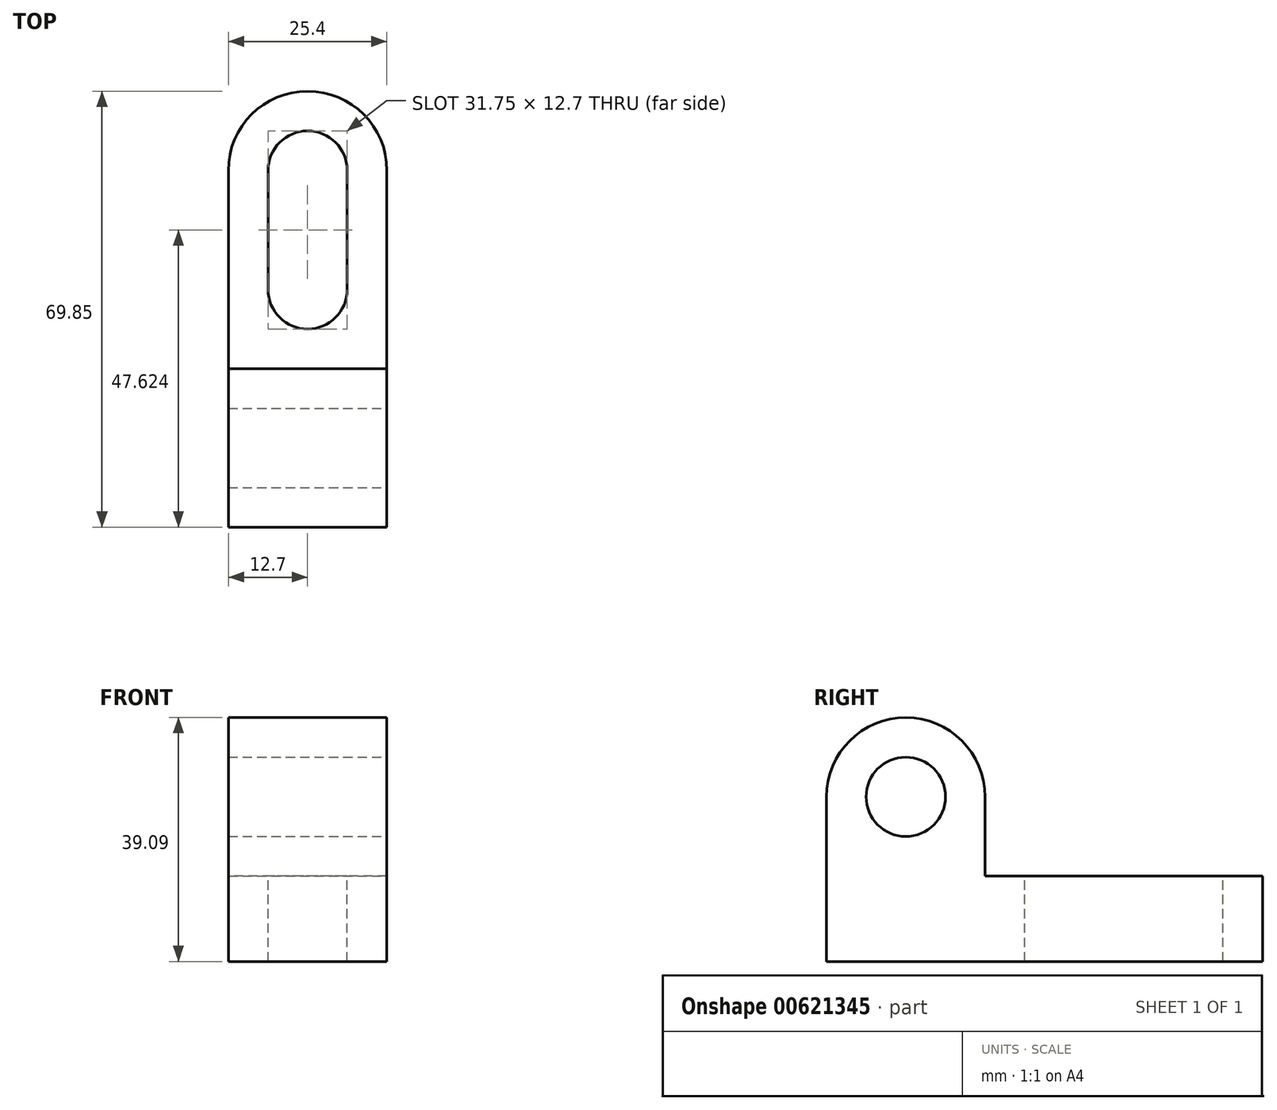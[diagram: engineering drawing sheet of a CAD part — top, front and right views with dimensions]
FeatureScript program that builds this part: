
annotation { "Feature Type Name" : "Feature", "Feature Type Description" : "" }
export const myFeature = defineFeature(function(context is Context, id is Id, definition is map)
    precondition{}
    {
        {
            var Q0;
            Q0=qCreatedBy(makeId("Right.planeOp"),FACE);
            var sketch = newSketch(context, id + "F0", { "sketchPlane" : qUnion([Q0])});
            skLineSegment(sketch, "E0", {"start": v(34.74, -29.93) * mm, "end": v(-35.11, -29.93) * mm});
            skLineSegment(sketch, "E1", {"start": v(-35.11, -29.93) * mm, "end": v(-35.11, 9.16) * mm});
            skLineSegment(sketch, "E2", {"start": v(-35.11, 9.16) * mm, "end": v(34.74, 9.16) * mm});
            skLineSegment(sketch, "E3", {"start": v(34.74, 9.16) * mm, "end": v(34.74, -29.93) * mm});
            skSolve(sketch);
        }
        {
            var Q0;
            Q0=makeQuery(id+"F0.imprint","IMPRINT",FACE,{"disambiguationData":[TD([[makeQuery(id+"F0.imprint","IMPRINT",EDGE,{"derivedFrom":sQuery(id+"F0.wireOp",EDGE,"E0")}),-1.0]])]});
            extrude(context, id + "F1", {"entities" : qUnion([Q0]), "depth" : 25.4 * mm, "offsetDistance" : 25.4 * mm});
        }
        {
            var Q0;
            Q0=makeQuery(id+"F1.opExtrude","CAP_FACE",FACE,{"disambiguationData":[OSD([sQuery(id+"F0.wireOp",EDGE,"E0"),sQuery(id+"F0.wireOp",EDGE,"E1"),sQuery(id+"F0.wireOp",EDGE,"E2"),sQuery(id+"F0.wireOp",EDGE,"E3")])],"isStart":false});
            var sketch = newSketch(context, id + "F2", { "sketchPlane" : qUnion([Q0])});
            skLineSegment(sketch, "E4", {"start": v(-9.71, 9.16) * mm, "end": v(-9.71, -16.24) * mm});
            skLineSegment(sketch, "E5", {"start": v(-9.71, -16.24) * mm, "end": v(34.74, -16.24) * mm});
            skLineSegment(sketch, "E6", {"start": v(34.74, -16.24) * mm, "end": v(34.74, 9.16) * mm});
            skLineSegment(sketch, "E7", {"start": v(34.74, 9.16) * mm, "end": v(-9.71, 9.16) * mm});
            skSolve(sketch);
        }
        {
            var Q0;
            Q0=makeQuery(id+"F2.imprint","IMPRINT",FACE,{"disambiguationData":[TD([[makeQuery(id+"F2.imprint","IMPRINT",EDGE,{"derivedFrom":sQuery(id+"F2.wireOp",EDGE,"E4")}),1.0]])]});
            extrude(context, id + "F3", {"entities" : qUnion([Q0]), "operationType" : NewBodyOperationType.REMOVE, "oppositeDirection" : true, "depth" : 25.4 * mm, "offsetDistance" : 25.4 * mm});
        }
        {
            var Q0;
            Q0=makeQuery(id+"F1.opExtrude","CAP_FACE",FACE,{"disambiguationData":[OSD([sQuery(id+"F0.wireOp",EDGE,"E0"),sQuery(id+"F0.wireOp",EDGE,"E1"),sQuery(id+"F0.wireOp",EDGE,"E2"),sQuery(id+"F0.wireOp",EDGE,"E3")])],"isStart":false});
            var sketch = newSketch(context, id + "F4", { "sketchPlane" : qUnion([Q0])});
            skLineSegment(sketch, "E8", {"start": v(-35.11, 9.16) * mm, "end": v(-35.11, -3.54) * mm});
            skLineSegment(sketch, "E9", {"start": v(-35.11, -3.54) * mm, "end": v(-9.71, -3.54) * mm});
            skCircle(sketch, "E10", {"center": v(-22.41, -3.54) * mm, "radius": 12.7 * mm});
            skCircle(sketch, "E11", {"center": v(-22.41, -3.54) * mm, "radius": 6.35 * mm});
            skSolve(sketch);
        }
        {
            var Q0;
            {var subQ1=makeQuery(id+"F3.boolean.opBoolean","COPY",EDGE,{"derivedFrom":makeQuery(id+"F3.opExtrude","CAP_EDGE",EDGE,{"disambiguationData":[OSD([sQuery(id+"F2.wireOp",EDGE,"E4")])],"isStart":true})});var subQ3=makeQuery(id+"F1.opExtrude","CAP_EDGE",EDGE,{"disambiguationData":[OSD([sQuery(id+"F0.wireOp",EDGE,"E2")])],"isStart":false});var subQ5=makeQuery(id+"F4.imprint","INTERSECT",VERTEX,{"derivedFrom":[subQ1,subQ3]});Q0=makeQuery(id+"F4.imprint","IMPRINT",FACE,{"disambiguationData":[TD([[makeQuery(id+"F4.imprint","IMPRINT",EDGE,{"disambiguationData":[TD([[subQ5,1.0]])],"derivedFrom":subQ3}),-1.0]])]});}
            var Q1;
            {var subQ0=sQuery(id+"F4.wireOp",EDGE,"E8");Q1=makeQuery(id+"F4.imprint","IMPRINT",FACE,{"disambiguationData":[TD([[makeQuery(id+"F4.imprint","IMPRINT",EDGE,{"derivedFrom":subQ0}),-1.0]])]});}
            var Q2;
            {var subQ0=sQuery(id+"F4.wireOp",EDGE,"E11");var subQ1=sQuery(id+"F4.wireOp",EDGE,"E9");var subQ2=makeQuery(id+"F4.imprint","INTERSECT",VERTEX,{"disambiguationData":[OD(0.0)],"derivedFrom":[subQ1,subQ0]});Q2=makeQuery(id+"F4.imprint","IMPRINT",FACE,{"disambiguationData":[TD([[makeQuery(id+"F4.imprint","IMPRINT",EDGE,{"disambiguationData":[TD([[subQ2,-1.0]])],"derivedFrom":subQ1}),1.0]])]});}
            var Q3;
            {var subQ0=sQuery(id+"F4.wireOp",EDGE,"E11");var subQ1=sQuery(id+"F4.wireOp",EDGE,"E9");var subQ2=makeQuery(id+"F4.imprint","INTERSECT",VERTEX,{"disambiguationData":[OD(0.0)],"derivedFrom":[subQ1,subQ0]});Q3=makeQuery(id+"F4.imprint","IMPRINT",FACE,{"disambiguationData":[TD([[makeQuery(id+"F4.imprint","IMPRINT",EDGE,{"disambiguationData":[TD([[subQ2,-1.0]])],"derivedFrom":subQ1}),-1.0]])]});}
            extrude(context, id + "F5", {"entities" : qUnion([Q0, Q1, Q2, Q3]), "operationType" : NewBodyOperationType.REMOVE, "oppositeDirection" : true, "depth" : 25.4 * mm, "offsetDistance" : 25.4 * mm});
        }
        {
            var Q0;
            Q0=makeQuery(id+"F3.boolean.opBoolean","COPY",FACE,{"derivedFrom":makeQuery(id+"F3.opExtrude","SWEPT_FACE",FACE,{"disambiguationData":[OSD([sQuery(id+"F2.wireOp",EDGE,"E5")])]})});
            var sketch = newSketch(context, id + "F6", { "sketchPlane" : qUnion([Q0])});
            skLineSegment(sketch, "E12", {"start": v(0, 34.74) * mm, "end": v(0, 22.04) * mm});
            skLineSegment(sketch, "E13", {"start": v(0, 22.04) * mm, "end": v(25.4, 22.04) * mm});
            skArc(sketch, "E14", {"start": v(19.05, 11.04) * mm, "mid": v(12.7, 34.74) * mm, "end": v(6.35, 11.04) * mm});
            skArc(sketch, "E15", {"start": v(19.05, 22.04) * mm, "mid": v(12.7, 28.39) * mm, "end": v(6.35, 22.04) * mm});
            skLineSegment(sketch, "E16", {"start": v(0, -9.71) * mm, "end": v(0, 2.99) * mm});
            skLineSegment(sketch, "E17", {"start": v(0, 2.99) * mm, "end": v(25.4, 2.99) * mm});
            skArc(sketch, "E18", {"start": v(6.35, 2.99) * mm, "mid": v(12.7, -3.36) * mm, "end": v(19.05, 2.99) * mm});
            skLineSegment(sketch, "E19", {"start": v(6.35, 22.04) * mm, "end": v(6.35, 2.99) * mm});
            skLineSegment(sketch, "E20", {"start": v(19.05, 22.04) * mm, "end": v(19.05, 2.99) * mm});
            skSolve(sketch);
        }
        {
            var Q0;
            {var subQ0=sQuery(id+"F6.wireOp",EDGE,"E12");Q0=makeQuery(id+"F6.imprint","IMPRINT",FACE,{"disambiguationData":[TD([[makeQuery(id+"F6.imprint","IMPRINT",EDGE,{"derivedFrom":subQ0}),-1.0]])]});}
            var Q1;
            {var subQ0=sQuery(id+"F6.wireOp",EDGE,"E14");var subQ1=sQuery(id+"F2.wireOp",EDGE,"E5");var subQ2=makeQuery(id+"F3.boolean.opBoolean","COPY",EDGE,{"derivedFrom":makeQuery(id+"F3.opExtrude","CAP_EDGE",EDGE,{"disambiguationData":[OSD([subQ1])],"isStart":true})});var subQ3=makeQuery(id+"F6.imprint","INTERSECT",VERTEX,{"derivedFrom":[subQ2,sQuery(id+"F6.wireOp",EDGE,"E13"),subQ0]});Q1=makeQuery(id+"F6.imprint","IMPRINT",FACE,{"disambiguationData":[TD([[makeQuery(id+"F6.imprint","IMPRINT",EDGE,{"disambiguationData":[TD([[subQ3,-1.0]])],"derivedFrom":subQ0}),-1.0]])]});}
            var Q2;
            {var subQ0=sQuery(id+"F6.wireOp",EDGE,"E15");Q2=makeQuery(id+"F6.imprint","IMPRINT",FACE,{"disambiguationData":[TD([[makeQuery(id+"F6.imprint","IMPRINT",EDGE,{"derivedFrom":subQ0}),1.0]])]});}
            var Q3;
            {var subQ0=sQuery(id+"F6.wireOp",EDGE,"E19");var subQ1=sQuery(id+"F6.wireOp",EDGE,"E14");var subQ2=makeQuery(id+"F6.imprint","INTERSECT",VERTEX,{"derivedFrom":[subQ1,subQ0]});Q3=makeQuery(id+"F6.imprint","IMPRINT",FACE,{"disambiguationData":[TD([[makeQuery(id+"F6.imprint","IMPRINT",EDGE,{"disambiguationData":[TD([[subQ2,1.0]])],"derivedFrom":subQ0}),1.0]])]});}
            var Q4;
            {var subQ0=sQuery(id+"F6.wireOp",EDGE,"E18");Q4=makeQuery(id+"F6.imprint","IMPRINT",FACE,{"disambiguationData":[TD([[makeQuery(id+"F6.imprint","IMPRINT",EDGE,{"derivedFrom":subQ0}),1.0]])]});}
            extrude(context, id + "F7", {"entities" : qUnion([Q0, Q1, Q2, Q3, Q4]), "operationType" : NewBodyOperationType.REMOVE, "oppositeDirection" : true, "depth" : 25.4 * mm, "offsetDistance" : 25.4 * mm});
        }
    });
